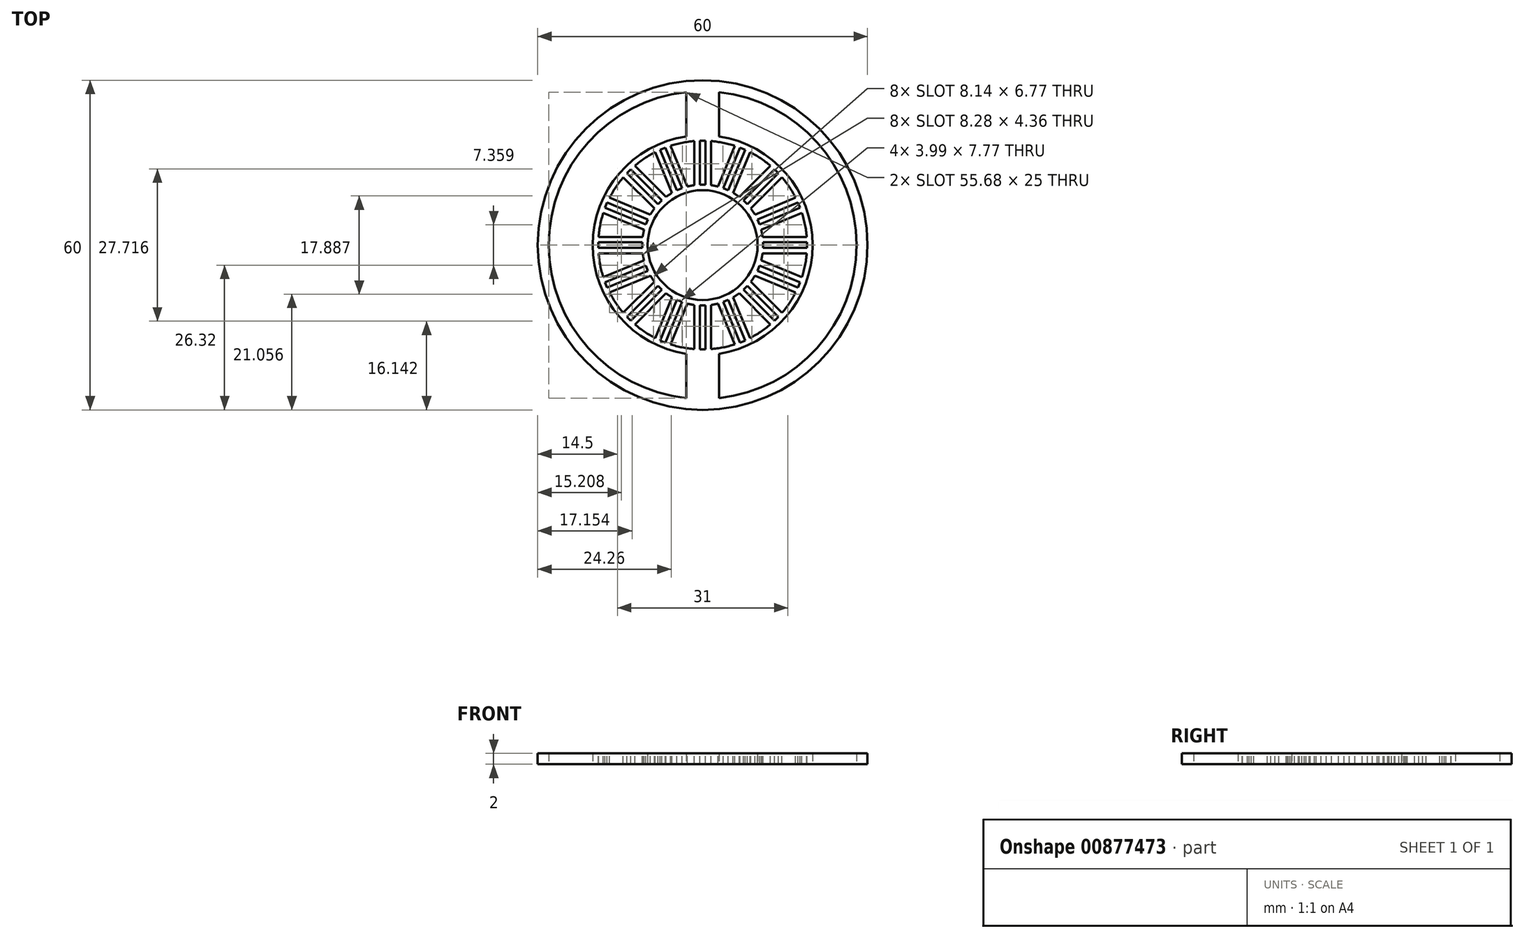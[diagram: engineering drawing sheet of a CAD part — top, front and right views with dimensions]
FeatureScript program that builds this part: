
annotation { "Feature Type Name" : "Feature", "Feature Type Description" : "" }
export const myFeature = defineFeature(function(context is Context, id is Id, definition is map)
    precondition{}
    {
        {
            var Q0;
            Q0=qCreatedBy(makeId("Top.planeOp"),FACE);
            var sketch = newSketch(context, id + "F0", { "sketchPlane" : qUnion([Q0])});
            skLineSegment(sketch, "E0", {"start": v(0, 41.56) * mm, "end": v(0, -42.56) * mm, "construction": true});
            skLineSegment(sketch, "E1", {"start": v(-3, 29.85) * mm, "end": v(-3, 19.77) * mm});
            skLineSegment(sketch, "E2.MirrorCS", {"start": v(3, 29.85) * mm, "end": v(3, 19.77) * mm});
            skArc(sketch, "E3", {"start": v(-3, -29.85) * mm, "mid": v(0, -30) * mm, "end": v(3, -29.85) * mm});
            skCircle(sketch, "E4", {"center": v(0, 0) * mm, "radius": 10 * mm});
            skArc(sketch, "E5.trimOffspring", {"start": v(3, 29.85) * mm, "mid": v(0, 30) * mm, "end": v(-3, 29.85) * mm});
            skArc(sketch, "E6", {"start": v(-3, 19.77) * mm, "mid": v(-13.78, 14.5) * mm, "end": v(-19.6, 4) * mm});
            skLineSegment(sketch, "E7.trimOffspring", {"start": v(-3, -19.77) * mm, "end": v(-3, -29.85) * mm});
            skLineSegment(sketch, "E8.trimOffspring", {"start": v(3, -19.77) * mm, "end": v(3, -29.85) * mm});
            skArc(sketch, "E9.trimOffspring", {"start": v(3, -19.77) * mm, "mid": v(13.78, -14.5) * mm, "end": v(19.6, -4) * mm});
            skLineSegment(sketch, "E10", {"start": v(-43.12, 0) * mm, "end": v(49.9, 0) * mm, "construction": true});
            skArc(sketch, "E11.trimOffspring", {"start": v(-19.6, -4) * mm, "mid": v(-13.78, -14.5) * mm, "end": v(-3, -19.77) * mm});
            skArc(sketch, "E12.trimOffspring", {"start": v(19.6, 4) * mm, "mid": v(13.78, 14.5) * mm, "end": v(3, 19.77) * mm});
            skArc(sketch, "E13", {"start": v(-19.6, 4) * mm, "mid": v(-20, 0) * mm, "end": v(-19.6, -4) * mm});
            skArc(sketch, "E14.trimOffspring", {"start": v(19.6, -4) * mm, "mid": v(20, 0) * mm, "end": v(19.6, 4) * mm});
            skSolve(sketch);
        }
        {
            var Q0;
            Q0 = qSketchRegion(id + "F0", true);
            extrude(context, id + "F1", {"entities" : qUnion([Q0]), "depth" : 2 * mm, "offsetDistance" : 25 * mm});
        }
        {
            var Q0;
            Q0=makeQuery(id+"F1.opExtrude","CAP_FACE",FACE,{"disambiguationData":[OSD([sQuery(id+"F0.wireOp",EDGE,"E1"),sQuery(id+"F0.wireOp",EDGE,"E2.MirrorCS"),sQuery(id+"F0.wireOp",EDGE,"E3"),sQuery(id+"F0.wireOp",EDGE,"E4"),sQuery(id+"F0.wireOp",EDGE,"E5.trimOffspring"),sQuery(id+"F0.wireOp",EDGE,"E6"),sQuery(id+"F0.wireOp",EDGE,"E7.trimOffspring"),sQuery(id+"F0.wireOp",EDGE,"E8.trimOffspring"),sQuery(id+"F0.wireOp",EDGE,"E9.trimOffspring"),sQuery(id+"F0.wireOp",EDGE,"E11.trimOffspring"),sQuery(id+"F0.wireOp",EDGE,"E12.trimOffspring"),sQuery(id+"F0.wireOp",EDGE,"E13"),sQuery(id+"F0.wireOp",EDGE,"E14.trimOffspring")])],"isStart":false});
            var sketch = newSketch(context, id + "F2", { "sketchPlane" : qUnion([Q0])});
            skLineSegment(sketch, "E15", {"start": v(0, 19.87) * mm, "end": v(0, -17.42) * mm, "construction": true});
            skLineSegment(sketch, "E16", {"start": v(-0.5, 19) * mm, "end": v(-0.5, 11) * mm});
            skLineSegment(sketch, "E17", {"start": v(-0.5, 11) * mm, "end": v(0, 11) * mm});
            skLineSegment(sketch, "E18", {"start": v(-0.5, 19) * mm, "end": v(0, 19) * mm});
            skCircle(sketch, "E19", {"center": v(0, 0) * mm, "radius": 15 * mm, "construction": true});
            skLineSegment(sketch, "E20.MirrorCS", {"start": v(0.5, 19) * mm, "end": v(0, 19) * mm});
            skLineSegment(sketch, "E21.MirrorCS", {"start": v(0.5, 19) * mm, "end": v(0.5, 11) * mm});
            skLineSegment(sketch, "E22.MirrorCS", {"start": v(0.5, 11) * mm, "end": v(0, 11) * mm});
            skLineSegment(sketch, "E23.1.0", {"start": v(7.73, 17.36) * mm, "end": v(7.27, 17.55) * mm});
            skLineSegment(sketch, "E23.1.1", {"start": v(7.73, 17.36) * mm, "end": v(4.67, 9.97) * mm});
            skLineSegment(sketch, "E23.1.2", {"start": v(6.8, 17.75) * mm, "end": v(7.27, 17.55) * mm});
            skLineSegment(sketch, "E23.1.3", {"start": v(6.8, 17.75) * mm, "end": v(3.75, 10.35) * mm});
            skLineSegment(sketch, "E23.1.4", {"start": v(3.75, 10.35) * mm, "end": v(4.2, 10.16) * mm});
            skLineSegment(sketch, "E23.1.5", {"start": v(4.67, 9.97) * mm, "end": v(4.2, 10.16) * mm});
            skLineSegment(sketch, "E23.2.0", {"start": v(13.79, 13.08) * mm, "end": v(13.44, 13.44) * mm});
            skLineSegment(sketch, "E23.2.1", {"start": v(13.79, 13.08) * mm, "end": v(8.13, 7.42) * mm});
            skLineSegment(sketch, "E23.2.2", {"start": v(13.08, 13.79) * mm, "end": v(13.44, 13.44) * mm});
            skLineSegment(sketch, "E23.2.3", {"start": v(13.08, 13.79) * mm, "end": v(7.42, 8.13) * mm});
            skLineSegment(sketch, "E23.2.4", {"start": v(7.42, 8.13) * mm, "end": v(7.78, 7.78) * mm});
            skLineSegment(sketch, "E23.2.5", {"start": v(8.13, 7.42) * mm, "end": v(7.78, 7.78) * mm});
            skLineSegment(sketch, "E23.3.0", {"start": v(17.75, 6.8) * mm, "end": v(17.55, 7.27) * mm});
            skLineSegment(sketch, "E23.3.1", {"start": v(17.75, 6.8) * mm, "end": v(10.35, 3.75) * mm});
            skLineSegment(sketch, "E23.3.2", {"start": v(17.36, 7.73) * mm, "end": v(17.55, 7.27) * mm});
            skLineSegment(sketch, "E23.3.3", {"start": v(17.36, 7.73) * mm, "end": v(9.97, 4.67) * mm});
            skLineSegment(sketch, "E23.3.4", {"start": v(9.97, 4.67) * mm, "end": v(10.16, 4.2) * mm});
            skLineSegment(sketch, "E23.3.5", {"start": v(10.35, 3.75) * mm, "end": v(10.16, 4.2) * mm});
            skLineSegment(sketch, "E23.4.0", {"start": v(19, -0.5) * mm, "end": v(19, 0) * mm});
            skLineSegment(sketch, "E23.4.1", {"start": v(19, -0.5) * mm, "end": v(11, -0.5) * mm});
            skLineSegment(sketch, "E23.4.2", {"start": v(19, 0.5) * mm, "end": v(19, 0) * mm});
            skLineSegment(sketch, "E23.4.3", {"start": v(19, 0.5) * mm, "end": v(11, 0.5) * mm});
            skLineSegment(sketch, "E23.4.4", {"start": v(11, 0.5) * mm, "end": v(11, 0) * mm});
            skLineSegment(sketch, "E23.4.5", {"start": v(11, -0.5) * mm, "end": v(11, 0) * mm});
            skLineSegment(sketch, "E23.5.0", {"start": v(17.36, -7.73) * mm, "end": v(17.55, -7.27) * mm});
            skLineSegment(sketch, "E23.5.1", {"start": v(17.36, -7.73) * mm, "end": v(9.97, -4.67) * mm});
            skLineSegment(sketch, "E23.5.2", {"start": v(17.75, -6.8) * mm, "end": v(17.55, -7.27) * mm});
            skLineSegment(sketch, "E23.5.3", {"start": v(17.75, -6.8) * mm, "end": v(10.35, -3.75) * mm});
            skLineSegment(sketch, "E23.5.4", {"start": v(10.35, -3.75) * mm, "end": v(10.16, -4.2) * mm});
            skLineSegment(sketch, "E23.5.5", {"start": v(9.97, -4.67) * mm, "end": v(10.16, -4.2) * mm});
            skLineSegment(sketch, "E23.6.0", {"start": v(13.08, -13.79) * mm, "end": v(13.44, -13.44) * mm});
            skLineSegment(sketch, "E23.6.1", {"start": v(13.08, -13.79) * mm, "end": v(7.42, -8.13) * mm});
            skLineSegment(sketch, "E23.6.2", {"start": v(13.79, -13.08) * mm, "end": v(13.44, -13.44) * mm});
            skLineSegment(sketch, "E23.6.3", {"start": v(13.79, -13.08) * mm, "end": v(8.13, -7.42) * mm});
            skLineSegment(sketch, "E23.6.4", {"start": v(8.13, -7.42) * mm, "end": v(7.78, -7.78) * mm});
            skLineSegment(sketch, "E23.6.5", {"start": v(7.42, -8.13) * mm, "end": v(7.78, -7.78) * mm});
            skLineSegment(sketch, "E23.7.0", {"start": v(6.8, -17.75) * mm, "end": v(7.27, -17.55) * mm});
            skLineSegment(sketch, "E23.7.1", {"start": v(6.8, -17.75) * mm, "end": v(3.75, -10.35) * mm});
            skLineSegment(sketch, "E23.7.2", {"start": v(7.73, -17.36) * mm, "end": v(7.27, -17.55) * mm});
            skLineSegment(sketch, "E23.7.3", {"start": v(7.73, -17.36) * mm, "end": v(4.67, -9.97) * mm});
            skLineSegment(sketch, "E23.7.4", {"start": v(4.67, -9.97) * mm, "end": v(4.2, -10.16) * mm});
            skLineSegment(sketch, "E23.7.5", {"start": v(3.75, -10.35) * mm, "end": v(4.2, -10.16) * mm});
            skLineSegment(sketch, "E23.8.0", {"start": v(-0.5, -19) * mm, "end": v(0, -19) * mm});
            skLineSegment(sketch, "E23.8.1", {"start": v(-0.5, -19) * mm, "end": v(-0.5, -11) * mm});
            skLineSegment(sketch, "E23.8.2", {"start": v(0.5, -19) * mm, "end": v(0, -19) * mm});
            skLineSegment(sketch, "E23.8.3", {"start": v(0.5, -19) * mm, "end": v(0.5, -11) * mm});
            skLineSegment(sketch, "E23.8.4", {"start": v(0.5, -11) * mm, "end": v(0, -11) * mm});
            skLineSegment(sketch, "E23.8.5", {"start": v(-0.5, -11) * mm, "end": v(0, -11) * mm});
            skLineSegment(sketch, "E23.anchor1", {"start": v(0, 0) * mm, "end": v(0, 19) * mm, "construction": true});
            skLineSegment(sketch, "E23.anchor2", {"start": v(0, 0) * mm, "end": v(0, -19) * mm, "construction": true});
            skLineSegment(sketch, "E24.MirrorCS", {"start": v(-13.79, 13.08) * mm, "end": v(-13.44, 13.44) * mm});
            skLineSegment(sketch, "E25.MirrorCS", {"start": v(-19, 0.5) * mm, "end": v(-19, 0) * mm});
            skLineSegment(sketch, "E26.MirrorCS", {"start": v(-7.42, 8.13) * mm, "end": v(-7.78, 7.78) * mm});
            skLineSegment(sketch, "E27.MirrorCS", {"start": v(-17.75, -6.8) * mm, "end": v(-17.55, -7.27) * mm});
            skLineSegment(sketch, "E28.MirrorCS", {"start": v(-13.08, 13.79) * mm, "end": v(-13.44, 13.44) * mm});
            skLineSegment(sketch, "E29.MirrorCS", {"start": v(-8.13, -7.42) * mm, "end": v(-7.78, -7.78) * mm});
            skLineSegment(sketch, "E30.MirrorCS", {"start": v(-13.79, -13.08) * mm, "end": v(-13.44, -13.44) * mm});
            skLineSegment(sketch, "E31.MirrorCS", {"start": v(-17.75, 6.8) * mm, "end": v(-17.55, 7.27) * mm});
            skLineSegment(sketch, "E32.MirrorCS", {"start": v(-19, -0.5) * mm, "end": v(-19, 0) * mm});
            skLineSegment(sketch, "E33.MirrorCS", {"start": v(-13.08, -13.79) * mm, "end": v(-13.44, -13.44) * mm});
            skLineSegment(sketch, "E34.MirrorCS", {"start": v(-11, 0.5) * mm, "end": v(-11, 0) * mm});
            skLineSegment(sketch, "E35.MirrorCS", {"start": v(-6.8, -17.75) * mm, "end": v(-7.27, -17.55) * mm});
            skLineSegment(sketch, "E36.MirrorCS", {"start": v(-10.35, -3.75) * mm, "end": v(-10.16, -4.2) * mm});
            skLineSegment(sketch, "E37.MirrorCS", {"start": v(-7.73, 17.36) * mm, "end": v(-7.27, 17.55) * mm});
            skLineSegment(sketch, "E38.MirrorCS", {"start": v(-9.97, 4.67) * mm, "end": v(-10.16, 4.2) * mm});
            skLineSegment(sketch, "E39.MirrorCS", {"start": v(-9.97, -4.67) * mm, "end": v(-10.16, -4.2) * mm});
            skLineSegment(sketch, "E40.MirrorCS", {"start": v(-10.35, 3.75) * mm, "end": v(-10.16, 4.2) * mm});
            skLineSegment(sketch, "E41.MirrorCS", {"start": v(-7.73, -17.36) * mm, "end": v(-7.27, -17.55) * mm});
            skLineSegment(sketch, "E42.MirrorCS", {"start": v(-8.13, 7.42) * mm, "end": v(-7.78, 7.78) * mm});
            skLineSegment(sketch, "E43.MirrorCS", {"start": v(-7.42, -8.13) * mm, "end": v(-7.78, -7.78) * mm});
            skLineSegment(sketch, "E44.MirrorCS", {"start": v(-17.36, 7.73) * mm, "end": v(-17.55, 7.27) * mm});
            skLineSegment(sketch, "E45.MirrorCS", {"start": v(-11, -0.5) * mm, "end": v(-11, 0) * mm});
            skLineSegment(sketch, "E46.MirrorCS", {"start": v(-6.8, 17.75) * mm, "end": v(-7.27, 17.55) * mm});
            skLineSegment(sketch, "E47.MirrorCS", {"start": v(-17.36, -7.73) * mm, "end": v(-17.55, -7.27) * mm});
            skLineSegment(sketch, "E48.MirrorCS", {"start": v(-17.36, 7.73) * mm, "end": v(-9.97, 4.67) * mm});
            skLineSegment(sketch, "E49.MirrorCS", {"start": v(-13.79, -13.08) * mm, "end": v(-8.13, -7.42) * mm});
            skLineSegment(sketch, "E50.MirrorCS", {"start": v(-17.75, -6.8) * mm, "end": v(-10.35, -3.75) * mm});
            skLineSegment(sketch, "E51.MirrorCS", {"start": v(-19, 0.5) * mm, "end": v(-11, 0.5) * mm});
            skLineSegment(sketch, "E52.MirrorCS", {"start": v(-7.73, -17.36) * mm, "end": v(-4.67, -9.97) * mm});
            skLineSegment(sketch, "E53.MirrorCS", {"start": v(-17.75, 6.8) * mm, "end": v(-10.35, 3.75) * mm});
            skLineSegment(sketch, "E54.MirrorCS", {"start": v(-17.36, -7.73) * mm, "end": v(-9.97, -4.67) * mm});
            skLineSegment(sketch, "E55.MirrorCS", {"start": v(-7.73, 17.36) * mm, "end": v(-4.67, 9.97) * mm});
            skLineSegment(sketch, "E56.MirrorCS", {"start": v(-13.08, 13.79) * mm, "end": v(-7.42, 8.13) * mm});
            skLineSegment(sketch, "E57.MirrorCS", {"start": v(-19, -0.5) * mm, "end": v(-11, -0.5) * mm});
            skLineSegment(sketch, "E58.MirrorCS", {"start": v(-13.79, 13.08) * mm, "end": v(-8.13, 7.42) * mm});
            skLineSegment(sketch, "E59.MirrorCS", {"start": v(-13.08, -13.79) * mm, "end": v(-7.42, -8.13) * mm});
            skLineSegment(sketch, "E60.MirrorCS", {"start": v(-6.8, 17.75) * mm, "end": v(-3.75, 10.35) * mm});
            skLineSegment(sketch, "E61.MirrorCS", {"start": v(-3.75, 10.35) * mm, "end": v(-4.2, 10.16) * mm});
            skLineSegment(sketch, "E62.MirrorCS", {"start": v(-4.67, 9.97) * mm, "end": v(-4.2, 10.16) * mm});
            skLineSegment(sketch, "E63.MirrorCS", {"start": v(-3.75, -10.35) * mm, "end": v(-4.2, -10.16) * mm});
            skLineSegment(sketch, "E64.MirrorCS", {"start": v(-4.67, -9.97) * mm, "end": v(-4.2, -10.16) * mm});
            skLineSegment(sketch, "E65.MirrorCS", {"start": v(-6.8, -17.75) * mm, "end": v(-3.75, -10.35) * mm});
            skSolve(sketch);
        }
        {
            var Q0;
            Q0 = qSketchRegion(id + "F2", true);
            extrude(context, id + "F3", {"entities" : qUnion([Q0]), "operationType" : NewBodyOperationType.REMOVE, "oppositeDirection" : true, "depth" : 25 * mm, "offsetDistance" : 25 * mm});
        }
        {
            var Q0;
            Q0=makeQuery(id+"F1.opExtrude","CAP_FACE",FACE,{"disambiguationData":[OSD([sQuery(id+"F0.wireOp",EDGE,"E1"),sQuery(id+"F0.wireOp",EDGE,"E2.MirrorCS"),sQuery(id+"F0.wireOp",EDGE,"E3"),sQuery(id+"F0.wireOp",EDGE,"E4"),sQuery(id+"F0.wireOp",EDGE,"E5.trimOffspring"),sQuery(id+"F0.wireOp",EDGE,"E6"),sQuery(id+"F0.wireOp",EDGE,"E7.trimOffspring"),sQuery(id+"F0.wireOp",EDGE,"E8.trimOffspring"),sQuery(id+"F0.wireOp",EDGE,"E9.trimOffspring"),sQuery(id+"F0.wireOp",EDGE,"E11.trimOffspring"),sQuery(id+"F0.wireOp",EDGE,"E12.trimOffspring"),sQuery(id+"F0.wireOp",EDGE,"E13"),sQuery(id+"F0.wireOp",EDGE,"E14.trimOffspring")])],"isStart":false});
            var sketch = newSketch(context, id + "F4", { "sketchPlane" : qUnion([Q0])});
            skArc(sketch, "E66", {"start": v(-1.5, 10.9) * mm, "mid": v(-2.15, 10.8) * mm, "end": v(-2.79, 10.65) * mm});
            skLineSegment(sketch, "E67", {"start": v(-1.5, 10.9) * mm, "end": v(-1.5, 18.93) * mm});
            skLineSegment(sketch, "E68", {"start": v(-2.79, 10.65) * mm, "end": v(-5.86, 18.07) * mm});
            skArc(sketch, "E69", {"start": v(-1.5, 18.93) * mm, "mid": v(-3.7, 18.63) * mm, "end": v(-5.86, 18.07) * mm});
            skArc(sketch, "E70.1.0", {"start": v(5.86, 18.07) * mm, "mid": v(3.7, 18.63) * mm, "end": v(1.5, 18.93) * mm});
            skLineSegment(sketch, "E70.1.1", {"start": v(2.79, 10.65) * mm, "end": v(5.86, 18.07) * mm});
            skArc(sketch, "E70.1.2", {"start": v(2.79, 10.65) * mm, "mid": v(2.15, 10.8) * mm, "end": v(1.5, 10.9) * mm});
            skLineSegment(sketch, "E70.1.3", {"start": v(1.5, 10.9) * mm, "end": v(1.5, 18.93) * mm});
            skArc(sketch, "E70.2.0", {"start": v(12.33, 14.45) * mm, "mid": v(10.55, 15.8) * mm, "end": v(8.63, 16.92) * mm});
            skLineSegment(sketch, "E70.2.1", {"start": v(6.65, 8.77) * mm, "end": v(12.33, 14.45) * mm});
            skArc(sketch, "E70.2.2", {"start": v(6.65, 8.77) * mm, "mid": v(6.12, 9.16) * mm, "end": v(5.56, 9.5) * mm});
            skLineSegment(sketch, "E70.2.3", {"start": v(5.56, 9.5) * mm, "end": v(8.63, 16.92) * mm});
            skArc(sketch, "E70.3.0", {"start": v(16.92, 8.63) * mm, "mid": v(15.8, 10.55) * mm, "end": v(14.45, 12.33) * mm});
            skLineSegment(sketch, "E70.3.1", {"start": v(9.5, 5.56) * mm, "end": v(16.92, 8.63) * mm});
            skArc(sketch, "E70.3.2", {"start": v(9.5, 5.56) * mm, "mid": v(9.16, 6.12) * mm, "end": v(8.77, 6.65) * mm});
            skLineSegment(sketch, "E70.3.3", {"start": v(8.77, 6.65) * mm, "end": v(14.45, 12.33) * mm});
            skArc(sketch, "E70.4.0", {"start": v(18.93, 1.5) * mm, "mid": v(18.63, 3.7) * mm, "end": v(18.07, 5.86) * mm});
            skLineSegment(sketch, "E70.4.1", {"start": v(10.9, 1.5) * mm, "end": v(18.93, 1.5) * mm});
            skArc(sketch, "E70.4.2", {"start": v(10.9, 1.5) * mm, "mid": v(10.8, 2.15) * mm, "end": v(10.65, 2.79) * mm});
            skLineSegment(sketch, "E70.4.3", {"start": v(10.65, 2.79) * mm, "end": v(18.07, 5.86) * mm});
            skArc(sketch, "E70.5.0", {"start": v(18.07, -5.86) * mm, "mid": v(18.63, -3.7) * mm, "end": v(18.93, -1.5) * mm});
            skLineSegment(sketch, "E70.5.1", {"start": v(10.65, -2.79) * mm, "end": v(18.07, -5.86) * mm});
            skArc(sketch, "E70.5.2", {"start": v(10.65, -2.79) * mm, "mid": v(10.8, -2.15) * mm, "end": v(10.9, -1.5) * mm});
            skLineSegment(sketch, "E70.5.3", {"start": v(10.9, -1.5) * mm, "end": v(18.93, -1.5) * mm});
            skArc(sketch, "E70.6.0", {"start": v(14.45, -12.33) * mm, "mid": v(15.8, -10.55) * mm, "end": v(16.92, -8.63) * mm});
            skLineSegment(sketch, "E70.6.1", {"start": v(8.77, -6.65) * mm, "end": v(14.45, -12.33) * mm});
            skArc(sketch, "E70.6.2", {"start": v(8.77, -6.65) * mm, "mid": v(9.16, -6.12) * mm, "end": v(9.5, -5.56) * mm});
            skLineSegment(sketch, "E70.6.3", {"start": v(9.5, -5.56) * mm, "end": v(16.92, -8.63) * mm});
            skArc(sketch, "E70.7.0", {"start": v(8.63, -16.92) * mm, "mid": v(10.55, -15.8) * mm, "end": v(12.33, -14.45) * mm});
            skLineSegment(sketch, "E70.7.1", {"start": v(5.56, -9.5) * mm, "end": v(8.63, -16.92) * mm});
            skArc(sketch, "E70.7.2", {"start": v(5.56, -9.5) * mm, "mid": v(6.12, -9.16) * mm, "end": v(6.65, -8.77) * mm});
            skLineSegment(sketch, "E70.7.3", {"start": v(6.65, -8.77) * mm, "end": v(12.33, -14.45) * mm});
            skArc(sketch, "E70.8.0", {"start": v(1.5, -18.93) * mm, "mid": v(3.7, -18.63) * mm, "end": v(5.86, -18.07) * mm});
            skLineSegment(sketch, "E70.8.1", {"start": v(1.5, -10.9) * mm, "end": v(1.5, -18.93) * mm});
            skArc(sketch, "E70.8.2", {"start": v(1.5, -10.9) * mm, "mid": v(2.15, -10.8) * mm, "end": v(2.79, -10.65) * mm});
            skLineSegment(sketch, "E70.8.3", {"start": v(2.79, -10.65) * mm, "end": v(5.86, -18.07) * mm});
            skLineSegment(sketch, "E70.anchor1", {"start": v(0, 0) * mm, "end": v(-5.86, 18.07) * mm, "construction": true});
            skLineSegment(sketch, "E70.anchor2", {"start": v(0, 0) * mm, "end": v(5.86, -18.07) * mm, "construction": true});
            skLineSegment(sketch, "E71", {"start": v(0, 24.57) * mm, "end": v(0, -24.9) * mm, "construction": true});
            skPoint(sketch, "E71.startSnap0", {"position": v(0, 30) * mm});
            skArc(sketch, "E72.MirrorCS", {"start": v(-12.33, 14.45) * mm, "mid": v(-10.55, 15.8) * mm, "end": v(-8.63, 16.92) * mm});
            skArc(sketch, "E73.MirrorCS", {"start": v(-10.9, 1.5) * mm, "mid": v(-10.8, 2.15) * mm, "end": v(-10.65, 2.79) * mm});
            skArc(sketch, "E74.MirrorCS", {"start": v(-8.77, -6.65) * mm, "mid": v(-9.16, -6.12) * mm, "end": v(-9.5, -5.56) * mm});
            skArc(sketch, "E75.MirrorCS", {"start": v(-10.65, -2.79) * mm, "mid": v(-10.8, -2.15) * mm, "end": v(-10.9, -1.5) * mm});
            skArc(sketch, "E76.MirrorCS", {"start": v(-9.5, 5.56) * mm, "mid": v(-9.16, 6.12) * mm, "end": v(-8.77, 6.65) * mm});
            skLineSegment(sketch, "E77.MirrorCS", {"start": v(-10.9, 1.5) * mm, "end": v(-18.93, 1.5) * mm});
            skLineSegment(sketch, "E78.MirrorCS", {"start": v(-8.77, -6.65) * mm, "end": v(-14.45, -12.33) * mm});
            skLineSegment(sketch, "E79.MirrorCS", {"start": v(-9.5, -5.56) * mm, "end": v(-16.92, -8.63) * mm});
            skArc(sketch, "E80.MirrorCS", {"start": v(-8.63, -16.92) * mm, "mid": v(-10.55, -15.8) * mm, "end": v(-12.33, -14.45) * mm});
            skArc(sketch, "E81.MirrorCS", {"start": v(-16.92, 8.63) * mm, "mid": v(-15.8, 10.55) * mm, "end": v(-14.45, 12.33) * mm});
            skLineSegment(sketch, "E82.MirrorCS", {"start": v(-10.65, -2.79) * mm, "end": v(-18.07, -5.86) * mm});
            skArc(sketch, "E83.MirrorCS", {"start": v(-14.45, -12.33) * mm, "mid": v(-15.8, -10.55) * mm, "end": v(-16.92, -8.63) * mm});
            skArc(sketch, "E84.MirrorCS", {"start": v(-18.93, 1.5) * mm, "mid": v(-18.63, 3.7) * mm, "end": v(-18.07, 5.86) * mm});
            skLineSegment(sketch, "E85.MirrorCS", {"start": v(-8.77, 6.65) * mm, "end": v(-14.45, 12.33) * mm});
            skLineSegment(sketch, "E86.MirrorCS", {"start": v(-10.65, 2.79) * mm, "end": v(-18.07, 5.86) * mm});
            skLineSegment(sketch, "E87.MirrorCS", {"start": v(-10.9, -1.5) * mm, "end": v(-18.93, -1.5) * mm});
            skLineSegment(sketch, "E88.MirrorCS", {"start": v(-9.5, 5.56) * mm, "end": v(-16.92, 8.63) * mm});
            skArc(sketch, "E89.MirrorCS", {"start": v(-18.07, -5.86) * mm, "mid": v(-18.63, -3.7) * mm, "end": v(-18.93, -1.5) * mm});
            skLineSegment(sketch, "E90.MirrorCS", {"start": v(-5.56, 9.5) * mm, "end": v(-8.63, 16.92) * mm});
            skLineSegment(sketch, "E91.MirrorCS", {"start": v(-6.65, 8.77) * mm, "end": v(-12.33, 14.45) * mm});
            skArc(sketch, "E92.MirrorCS", {"start": v(-6.65, 8.77) * mm, "mid": v(-6.12, 9.16) * mm, "end": v(-5.56, 9.5) * mm});
            skArc(sketch, "E93.MirrorCS", {"start": v(-5.56, -9.5) * mm, "mid": v(-6.12, -9.16) * mm, "end": v(-6.65, -8.77) * mm});
            skLineSegment(sketch, "E94.MirrorCS", {"start": v(-6.65, -8.77) * mm, "end": v(-12.33, -14.45) * mm});
            skLineSegment(sketch, "E95.MirrorCS", {"start": v(-5.56, -9.5) * mm, "end": v(-8.63, -16.92) * mm});
            skLineSegment(sketch, "E96.MirrorCS", {"start": v(-2.79, -10.65) * mm, "end": v(-5.86, -18.07) * mm});
            skArc(sketch, "E97.MirrorCS", {"start": v(-1.5, -10.9) * mm, "mid": v(-2.15, -10.8) * mm, "end": v(-2.79, -10.65) * mm});
            skLineSegment(sketch, "E98.MirrorCS", {"start": v(-1.5, -10.9) * mm, "end": v(-1.5, -18.93) * mm});
            skArc(sketch, "E99.MirrorCS", {"start": v(-1.5, -18.93) * mm, "mid": v(-3.7, -18.63) * mm, "end": v(-5.86, -18.07) * mm});
            skSolve(sketch);
        }
        {
            var Q0;
            Q0 = qSketchRegion(id + "F4", true);
            extrude(context, id + "F5", {"entities" : qUnion([Q0]), "operationType" : NewBodyOperationType.REMOVE, "oppositeDirection" : true, "depth" : 25 * mm, "offsetDistance" : 25 * mm});
        }
        {
            var Q0;
            Q0=qCreatedBy(makeId("Top.planeOp"),FACE);
            var sketch = newSketch(context, id + "F6", { "sketchPlane" : qUnion([Q0])});
            skCircle(sketch, "E100", {"center": v(0, 0) * mm, "radius": 30 * mm});
            skCircle(sketch, "E101.0", {"center": v(0, 0) * mm, "radius": 28 * mm});
            skSolve(sketch);
        }
        {
            var Q0;
            Q0 = qSketchRegion(id + "F6", true);
            extrude(context, id + "F7", {"entities" : qUnion([Q0]), "operationType" : NewBodyOperationType.ADD, "depth" : 2 * mm, "offsetDistance" : 25 * mm});
        }
    });
